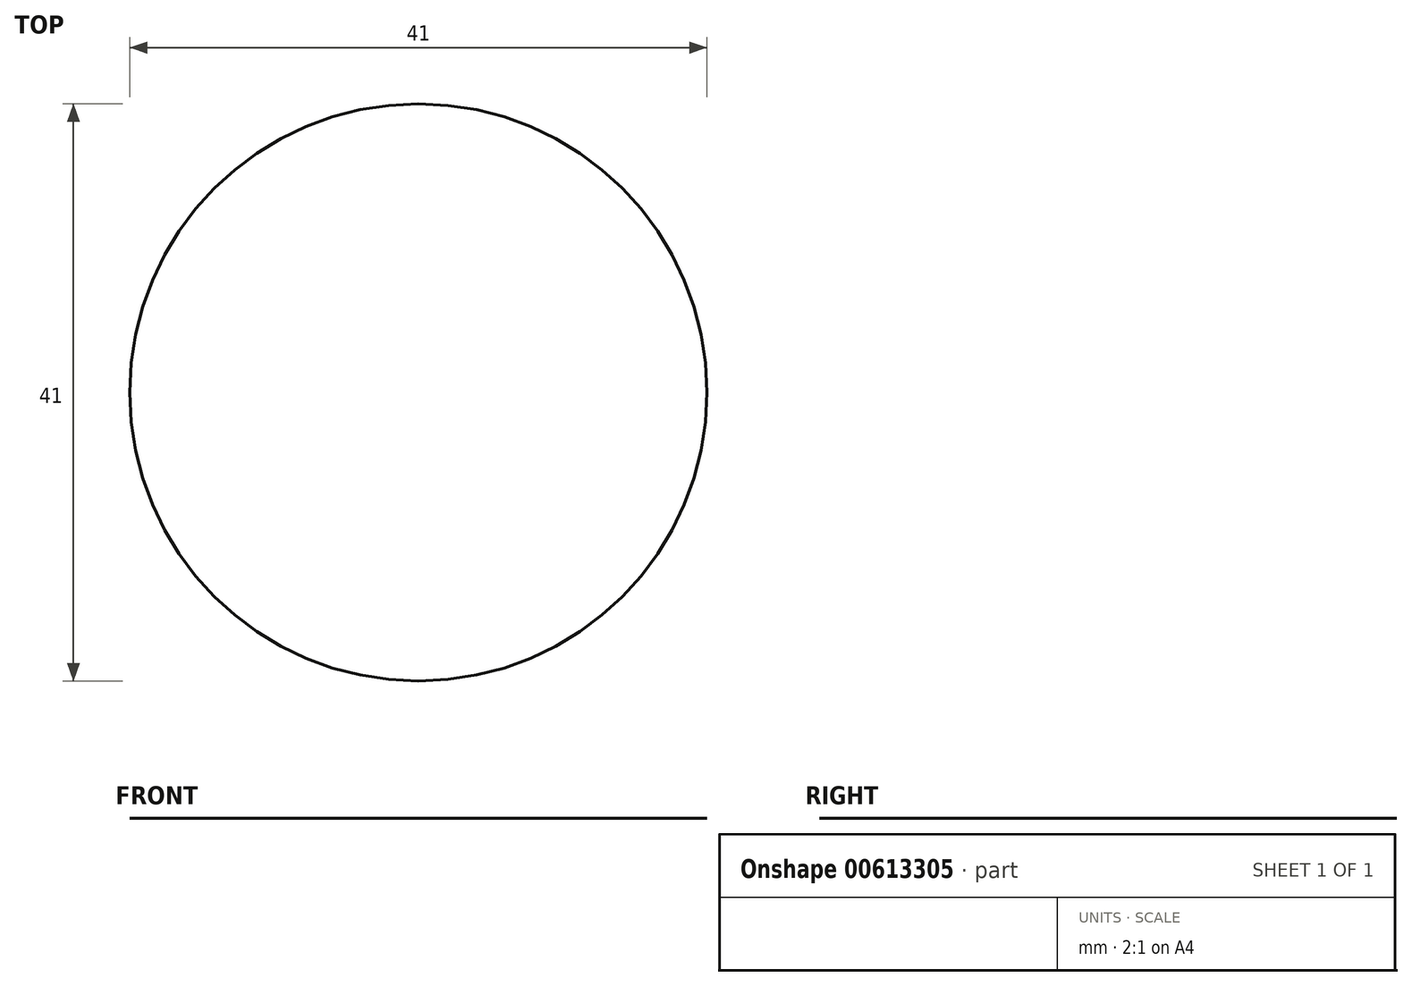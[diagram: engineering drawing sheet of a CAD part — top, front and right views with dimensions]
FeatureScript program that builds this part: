
annotation { "Feature Type Name" : "Feature", "Feature Type Description" : "" }
export const myFeature = defineFeature(function(context is Context, id is Id, definition is map)
    precondition{}
    {
        {
            var Q0;
            Q0=qCreatedBy(makeId("Top.planeOp"),FACE);
            var sketch = newSketch(context, id + "F0", { "sketchPlane" : qUnion([Q0])});
            skCircle(sketch, "E0", {"center": v(0, 0) * mm, "radius": 20.5 * mm});
            skSolve(sketch);
        }
        {
            var Q0;
            Q0 = qSketchRegion(id + "F0", true);
            var Q1;
            Q1 = qConstructionFilter(qBodyType(qCreatedBy(id + "F0" ,EDGE), BodyType.WIRE), ConstructionObject.NO);
            extrude(context, id + "F1", {"entities" : qUnion([Q0]), "surfaceEntities" : qUnion([Q1]), "depth" : 0 * mm, "offsetDistance" : 25 * mm});
        }
    });
